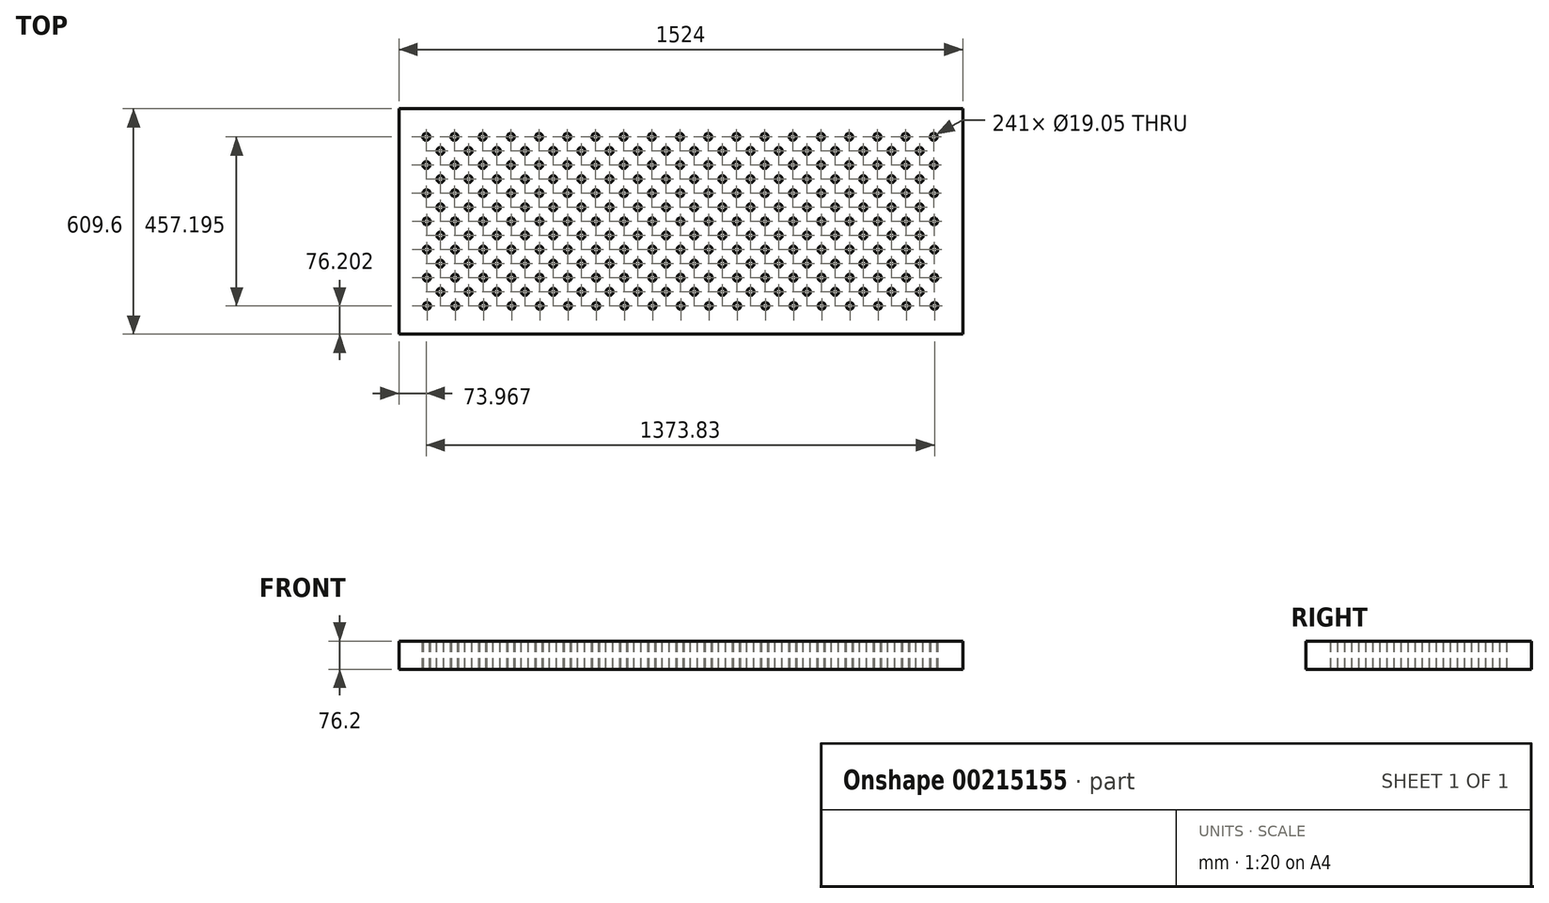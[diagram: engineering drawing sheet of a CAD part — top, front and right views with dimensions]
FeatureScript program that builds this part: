
annotation { "Feature Type Name" : "Feature", "Feature Type Description" : "" }
export const myFeature = defineFeature(function(context is Context, id is Id, definition is map)
    precondition{}
    {
        {
            var Q0;
            Q0=qCreatedBy(makeId("Top.planeOp"),FACE);
            var sketch = newSketch(context, id + "F0", { "sketchPlane" : qUnion([Q0])});
            skLineSegment(sketch, "E0.bottom", {"start": v(732.78, -488.74) * mm, "end": v(-791.22, -488.74) * mm});
            skLineSegment(sketch, "E0.top", {"start": v(732.78, 120.86) * mm, "end": v(-791.22, 120.86) * mm});
            skLineSegment(sketch, "E0.left", {"start": v(732.78, -488.74) * mm, "end": v(732.78, 120.86) * mm});
            skLineSegment(sketch, "E0.right", {"start": v(-791.22, -488.74) * mm, "end": v(-791.22, 120.86) * mm});
            skCircle(sketch, "E1", {"center": v(-715.02, -412.54) * mm, "radius": 9.53 * mm});
            skCircle(sketch, "E2.0.1.0", {"center": v(-715.4, -336.34) * mm, "radius": 9.53 * mm});
            skCircle(sketch, "E2.0.2.0", {"center": v(-715.77, -260.14) * mm, "radius": 9.53 * mm});
            skCircle(sketch, "E2.0.3.0", {"center": v(-716.14, -183.94) * mm, "radius": 9.53 * mm});
            skCircle(sketch, "E2.0.4.0", {"center": v(-716.5, -107.74) * mm, "radius": 9.53 * mm});
            skCircle(sketch, "E2.0.5.0", {"center": v(-716.88, -31.54) * mm, "radius": 9.53 * mm});
            skCircle(sketch, "E2.0.6.0", {"center": v(-717.25, 44.66) * mm, "radius": 9.53 * mm});
            skCircle(sketch, "E2.1.0.0", {"center": v(-638.82, -412.54) * mm, "radius": 9.53 * mm});
            skCircle(sketch, "E2.1.1.0", {"center": v(-639.2, -336.34) * mm, "radius": 9.53 * mm});
            skCircle(sketch, "E2.1.2.0", {"center": v(-639.57, -260.14) * mm, "radius": 9.53 * mm});
            skCircle(sketch, "E2.1.3.0", {"center": v(-639.94, -183.94) * mm, "radius": 9.53 * mm});
            skCircle(sketch, "E2.1.4.0", {"center": v(-640.3, -107.74) * mm, "radius": 9.53 * mm});
            skCircle(sketch, "E2.1.5.0", {"center": v(-640.68, -31.54) * mm, "radius": 9.53 * mm});
            skCircle(sketch, "E2.1.6.0", {"center": v(-641.05, 44.66) * mm, "radius": 9.53 * mm});
            skCircle(sketch, "E2.2.0.0", {"center": v(-562.62, -412.54) * mm, "radius": 9.53 * mm});
            skCircle(sketch, "E2.2.1.0", {"center": v(-563, -336.34) * mm, "radius": 9.53 * mm});
            skCircle(sketch, "E2.2.2.0", {"center": v(-563.37, -260.14) * mm, "radius": 9.53 * mm});
            skCircle(sketch, "E2.2.3.0", {"center": v(-563.74, -183.94) * mm, "radius": 9.53 * mm});
            skCircle(sketch, "E2.2.4.0", {"center": v(-564.1, -107.74) * mm, "radius": 9.53 * mm});
            skCircle(sketch, "E2.2.5.0", {"center": v(-564.48, -31.54) * mm, "radius": 9.53 * mm});
            skCircle(sketch, "E2.2.6.0", {"center": v(-564.85, 44.66) * mm, "radius": 9.53 * mm});
            skLineSegment(sketch, "E2.direction1", {"start": v(-715.02, -412.54) * mm, "end": v(-638.82, -412.54) * mm, "construction": true});
            skLineSegment(sketch, "E2.direction2", {"start": v(-715.02, -412.54) * mm, "end": v(-715.4, -336.34) * mm, "construction": true});
            skCircle(sketch, "E3.0.3.0", {"center": v(-486.42, -412.54) * mm, "radius": 9.53 * mm});
            skCircle(sketch, "E3.0.3.1", {"center": v(-486.8, -336.34) * mm, "radius": 9.53 * mm});
            skCircle(sketch, "E3.0.3.2", {"center": v(-487.17, -260.14) * mm, "radius": 9.53 * mm});
            skCircle(sketch, "E3.0.3.3", {"center": v(-487.54, -183.94) * mm, "radius": 9.53 * mm});
            skCircle(sketch, "E3.0.3.4", {"center": v(-487.9, -107.74) * mm, "radius": 9.53 * mm});
            skCircle(sketch, "E3.0.3.5", {"center": v(-488.28, -31.54) * mm, "radius": 9.53 * mm});
            skCircle(sketch, "E3.0.3.6", {"center": v(-488.65, 44.66) * mm, "radius": 9.53 * mm});
            skCircle(sketch, "E3.0.4.0", {"center": v(-410.22, -412.54) * mm, "radius": 9.53 * mm});
            skCircle(sketch, "E3.0.4.1", {"center": v(-410.6, -336.34) * mm, "radius": 9.53 * mm});
            skCircle(sketch, "E3.0.4.2", {"center": v(-410.97, -260.14) * mm, "radius": 9.53 * mm});
            skCircle(sketch, "E3.0.4.3", {"center": v(-411.34, -183.94) * mm, "radius": 9.53 * mm});
            skCircle(sketch, "E3.0.4.4", {"center": v(-411.7, -107.74) * mm, "radius": 9.53 * mm});
            skCircle(sketch, "E3.0.4.5", {"center": v(-412.08, -31.54) * mm, "radius": 9.53 * mm});
            skCircle(sketch, "E3.0.4.6", {"center": v(-412.45, 44.66) * mm, "radius": 9.53 * mm});
            skCircle(sketch, "E3.0.5.0", {"center": v(-334.02, -412.54) * mm, "radius": 9.53 * mm});
            skCircle(sketch, "E3.0.5.1", {"center": v(-334.4, -336.34) * mm, "radius": 9.53 * mm});
            skCircle(sketch, "E3.0.5.2", {"center": v(-334.77, -260.14) * mm, "radius": 9.53 * mm});
            skCircle(sketch, "E3.0.5.3", {"center": v(-335.14, -183.94) * mm, "radius": 9.53 * mm});
            skCircle(sketch, "E3.0.5.4", {"center": v(-335.5, -107.74) * mm, "radius": 9.53 * mm});
            skCircle(sketch, "E3.0.5.5", {"center": v(-335.88, -31.54) * mm, "radius": 9.53 * mm});
            skCircle(sketch, "E3.0.5.6", {"center": v(-336.25, 44.66) * mm, "radius": 9.53 * mm});
            skCircle(sketch, "E3.0.6.0", {"center": v(-257.82, -412.54) * mm, "radius": 9.53 * mm});
            skCircle(sketch, "E3.0.6.1", {"center": v(-258.2, -336.34) * mm, "radius": 9.53 * mm});
            skCircle(sketch, "E3.0.6.2", {"center": v(-258.57, -260.14) * mm, "radius": 9.53 * mm});
            skCircle(sketch, "E3.0.6.3", {"center": v(-258.94, -183.94) * mm, "radius": 9.53 * mm});
            skCircle(sketch, "E3.0.6.4", {"center": v(-259.3, -107.74) * mm, "radius": 9.53 * mm});
            skCircle(sketch, "E3.0.6.5", {"center": v(-259.68, -31.54) * mm, "radius": 9.53 * mm});
            skCircle(sketch, "E3.0.6.6", {"center": v(-260.05, 44.66) * mm, "radius": 9.53 * mm});
            skCircle(sketch, "E3.0.7.0", {"center": v(-181.62, -412.54) * mm, "radius": 9.53 * mm});
            skCircle(sketch, "E3.0.7.1", {"center": v(-182, -336.34) * mm, "radius": 9.53 * mm});
            skCircle(sketch, "E3.0.7.2", {"center": v(-182.37, -260.14) * mm, "radius": 9.53 * mm});
            skCircle(sketch, "E3.0.7.3", {"center": v(-182.74, -183.94) * mm, "radius": 9.53 * mm});
            skCircle(sketch, "E3.0.7.4", {"center": v(-183.1, -107.74) * mm, "radius": 9.53 * mm});
            skCircle(sketch, "E3.0.7.5", {"center": v(-183.48, -31.54) * mm, "radius": 9.53 * mm});
            skCircle(sketch, "E3.0.7.6", {"center": v(-183.85, 44.66) * mm, "radius": 9.53 * mm});
            skCircle(sketch, "E3.0.8.0", {"center": v(-105.42, -412.54) * mm, "radius": 9.53 * mm});
            skCircle(sketch, "E3.0.8.1", {"center": v(-105.8, -336.34) * mm, "radius": 9.53 * mm});
            skCircle(sketch, "E3.0.8.2", {"center": v(-106.17, -260.14) * mm, "radius": 9.53 * mm});
            skCircle(sketch, "E3.0.8.3", {"center": v(-106.54, -183.94) * mm, "radius": 9.53 * mm});
            skCircle(sketch, "E3.0.8.4", {"center": v(-106.9, -107.74) * mm, "radius": 9.53 * mm});
            skCircle(sketch, "E3.0.8.5", {"center": v(-107.28, -31.54) * mm, "radius": 9.53 * mm});
            skCircle(sketch, "E3.0.8.6", {"center": v(-107.65, 44.66) * mm, "radius": 9.53 * mm});
            skCircle(sketch, "E3.0.9.0", {"center": v(-29.22, -412.54) * mm, "radius": 9.53 * mm});
            skCircle(sketch, "E3.0.9.1", {"center": v(-29.6, -336.34) * mm, "radius": 9.53 * mm});
            skCircle(sketch, "E3.0.9.2", {"center": v(-29.97, -260.14) * mm, "radius": 9.53 * mm});
            skCircle(sketch, "E3.0.9.3", {"center": v(-30.34, -183.94) * mm, "radius": 9.53 * mm});
            skCircle(sketch, "E3.0.9.4", {"center": v(-30.7, -107.74) * mm, "radius": 9.53 * mm});
            skCircle(sketch, "E3.0.9.5", {"center": v(-31.08, -31.54) * mm, "radius": 9.53 * mm});
            skCircle(sketch, "E3.0.9.6", {"center": v(-31.45, 44.66) * mm, "radius": 9.53 * mm});
            skCircle(sketch, "E3.0.10.0", {"center": v(46.98, -412.54) * mm, "radius": 9.53 * mm});
            skCircle(sketch, "E3.0.10.1", {"center": v(46.6, -336.34) * mm, "radius": 9.53 * mm});
            skCircle(sketch, "E3.0.10.2", {"center": v(46.23, -260.14) * mm, "radius": 9.53 * mm});
            skCircle(sketch, "E3.0.10.3", {"center": v(45.86, -183.94) * mm, "radius": 9.53 * mm});
            skCircle(sketch, "E3.0.10.4", {"center": v(45.5, -107.74) * mm, "radius": 9.53 * mm});
            skCircle(sketch, "E3.0.10.5", {"center": v(45.12, -31.54) * mm, "radius": 9.53 * mm});
            skCircle(sketch, "E3.0.10.6", {"center": v(44.75, 44.66) * mm, "radius": 9.53 * mm});
            skCircle(sketch, "E3.0.11.0", {"center": v(123.18, -412.54) * mm, "radius": 9.53 * mm});
            skCircle(sketch, "E3.0.11.1", {"center": v(122.8, -336.34) * mm, "radius": 9.53 * mm});
            skCircle(sketch, "E3.0.11.2", {"center": v(122.43, -260.14) * mm, "radius": 9.53 * mm});
            skCircle(sketch, "E3.0.11.3", {"center": v(122.06, -183.94) * mm, "radius": 9.53 * mm});
            skCircle(sketch, "E3.0.11.4", {"center": v(121.7, -107.74) * mm, "radius": 9.53 * mm});
            skCircle(sketch, "E3.0.11.5", {"center": v(121.32, -31.54) * mm, "radius": 9.53 * mm});
            skCircle(sketch, "E3.0.11.6", {"center": v(120.95, 44.66) * mm, "radius": 9.53 * mm});
            skCircle(sketch, "E3.0.12.0", {"center": v(199.38, -412.54) * mm, "radius": 9.53 * mm});
            skCircle(sketch, "E3.0.12.1", {"center": v(199, -336.34) * mm, "radius": 9.53 * mm});
            skCircle(sketch, "E3.0.12.2", {"center": v(198.63, -260.14) * mm, "radius": 9.53 * mm});
            skCircle(sketch, "E3.0.12.3", {"center": v(198.26, -183.94) * mm, "radius": 9.53 * mm});
            skCircle(sketch, "E3.0.12.4", {"center": v(197.9, -107.74) * mm, "radius": 9.53 * mm});
            skCircle(sketch, "E3.0.12.5", {"center": v(197.52, -31.54) * mm, "radius": 9.53 * mm});
            skCircle(sketch, "E3.0.12.6", {"center": v(197.15, 44.66) * mm, "radius": 9.53 * mm});
            skCircle(sketch, "E3.0.13.0", {"center": v(275.58, -412.54) * mm, "radius": 9.53 * mm});
            skCircle(sketch, "E3.0.13.1", {"center": v(275.2, -336.34) * mm, "radius": 9.53 * mm});
            skCircle(sketch, "E3.0.13.2", {"center": v(274.83, -260.14) * mm, "radius": 9.53 * mm});
            skCircle(sketch, "E3.0.13.3", {"center": v(274.46, -183.94) * mm, "radius": 9.53 * mm});
            skCircle(sketch, "E3.0.13.4", {"center": v(274.1, -107.74) * mm, "radius": 9.53 * mm});
            skCircle(sketch, "E3.0.13.5", {"center": v(273.72, -31.54) * mm, "radius": 9.53 * mm});
            skCircle(sketch, "E3.0.13.6", {"center": v(273.35, 44.66) * mm, "radius": 9.53 * mm});
            skCircle(sketch, "E3.0.14.0", {"center": v(351.78, -412.54) * mm, "radius": 9.53 * mm});
            skCircle(sketch, "E3.0.14.1", {"center": v(351.4, -336.34) * mm, "radius": 9.53 * mm});
            skCircle(sketch, "E3.0.14.2", {"center": v(351.03, -260.14) * mm, "radius": 9.53 * mm});
            skCircle(sketch, "E3.0.14.3", {"center": v(350.66, -183.94) * mm, "radius": 9.53 * mm});
            skCircle(sketch, "E3.0.14.4", {"center": v(350.3, -107.74) * mm, "radius": 9.53 * mm});
            skCircle(sketch, "E3.0.14.5", {"center": v(349.92, -31.54) * mm, "radius": 9.53 * mm});
            skCircle(sketch, "E3.0.14.6", {"center": v(349.55, 44.66) * mm, "radius": 9.53 * mm});
            skCircle(sketch, "E3.0.15.0", {"center": v(427.98, -412.54) * mm, "radius": 9.53 * mm});
            skCircle(sketch, "E3.0.15.1", {"center": v(427.6, -336.34) * mm, "radius": 9.53 * mm});
            skCircle(sketch, "E3.0.15.2", {"center": v(427.23, -260.14) * mm, "radius": 9.53 * mm});
            skCircle(sketch, "E3.0.15.3", {"center": v(426.86, -183.94) * mm, "radius": 9.53 * mm});
            skCircle(sketch, "E3.0.15.4", {"center": v(426.5, -107.74) * mm, "radius": 9.53 * mm});
            skCircle(sketch, "E3.0.15.5", {"center": v(426.12, -31.54) * mm, "radius": 9.53 * mm});
            skCircle(sketch, "E3.0.15.6", {"center": v(425.75, 44.66) * mm, "radius": 9.53 * mm});
            skCircle(sketch, "E3.0.16.0", {"center": v(504.18, -412.54) * mm, "radius": 9.53 * mm});
            skCircle(sketch, "E3.0.16.1", {"center": v(503.8, -336.34) * mm, "radius": 9.53 * mm});
            skCircle(sketch, "E3.0.16.2", {"center": v(503.43, -260.14) * mm, "radius": 9.53 * mm});
            skCircle(sketch, "E3.0.16.3", {"center": v(503.06, -183.94) * mm, "radius": 9.53 * mm});
            skCircle(sketch, "E3.0.16.4", {"center": v(502.7, -107.74) * mm, "radius": 9.53 * mm});
            skCircle(sketch, "E3.0.16.5", {"center": v(502.32, -31.54) * mm, "radius": 9.53 * mm});
            skCircle(sketch, "E3.0.16.6", {"center": v(501.95, 44.66) * mm, "radius": 9.53 * mm});
            skCircle(sketch, "E3.0.17.0", {"center": v(580.38, -412.54) * mm, "radius": 9.53 * mm});
            skCircle(sketch, "E3.0.17.1", {"center": v(580, -336.34) * mm, "radius": 9.53 * mm});
            skCircle(sketch, "E3.0.17.2", {"center": v(579.63, -260.14) * mm, "radius": 9.53 * mm});
            skCircle(sketch, "E3.0.17.3", {"center": v(579.26, -183.94) * mm, "radius": 9.53 * mm});
            skCircle(sketch, "E3.0.17.4", {"center": v(578.9, -107.74) * mm, "radius": 9.53 * mm});
            skCircle(sketch, "E3.0.17.5", {"center": v(578.52, -31.54) * mm, "radius": 9.53 * mm});
            skCircle(sketch, "E3.0.17.6", {"center": v(578.15, 44.66) * mm, "radius": 9.53 * mm});
            skCircle(sketch, "E3.0.18.0", {"center": v(656.58, -412.54) * mm, "radius": 9.53 * mm});
            skCircle(sketch, "E3.0.18.1", {"center": v(656.2, -336.34) * mm, "radius": 9.53 * mm});
            skCircle(sketch, "E3.0.18.2", {"center": v(655.83, -260.14) * mm, "radius": 9.53 * mm});
            skCircle(sketch, "E3.0.18.3", {"center": v(655.46, -183.94) * mm, "radius": 9.53 * mm});
            skCircle(sketch, "E3.0.18.4", {"center": v(655.1, -107.74) * mm, "radius": 9.53 * mm});
            skCircle(sketch, "E3.0.18.5", {"center": v(654.72, -31.54) * mm, "radius": 9.53 * mm});
            skCircle(sketch, "E3.0.18.6", {"center": v(654.35, 44.66) * mm, "radius": 9.53 * mm});
            skLineSegment(sketch, "E4", {"start": v(-641.05, 44.66) * mm, "end": v(-716.88, -31.54) * mm, "construction": true});
            skLineSegment(sketch, "E5", {"start": v(-640.68, -31.54) * mm, "end": v(-717.25, 44.66) * mm, "construction": true});
            skCircle(sketch, "E6", {"center": v(-678.97, 6.56) * mm, "radius": 9.52 * mm});
            skCircle(sketch, "E7.0.1.0", {"center": v(-678.97, -69.64) * mm, "radius": 9.52 * mm});
            skCircle(sketch, "E7.0.2.0", {"center": v(-678.97, -145.84) * mm, "radius": 9.52 * mm});
            skCircle(sketch, "E7.0.3.0", {"center": v(-678.97, -222.04) * mm, "radius": 9.52 * mm});
            skCircle(sketch, "E7.0.4.0", {"center": v(-678.97, -298.24) * mm, "radius": 9.52 * mm});
            skCircle(sketch, "E7.0.5.0", {"center": v(-678.97, -374.44) * mm, "radius": 9.52 * mm});
            skCircle(sketch, "E7.1.0.0", {"center": v(-602.77, 6.56) * mm, "radius": 9.52 * mm});
            skCircle(sketch, "E7.1.1.0", {"center": v(-602.77, -69.64) * mm, "radius": 9.52 * mm});
            skCircle(sketch, "E7.1.2.0", {"center": v(-602.77, -145.84) * mm, "radius": 9.52 * mm});
            skCircle(sketch, "E7.1.3.0", {"center": v(-602.77, -222.04) * mm, "radius": 9.52 * mm});
            skCircle(sketch, "E7.1.4.0", {"center": v(-602.77, -298.24) * mm, "radius": 9.52 * mm});
            skCircle(sketch, "E7.1.5.0", {"center": v(-602.77, -374.44) * mm, "radius": 9.52 * mm});
            skCircle(sketch, "E7.2.0.0", {"center": v(-526.57, 6.56) * mm, "radius": 9.52 * mm});
            skCircle(sketch, "E7.2.1.0", {"center": v(-526.57, -69.64) * mm, "radius": 9.52 * mm});
            skCircle(sketch, "E7.2.2.0", {"center": v(-526.57, -145.84) * mm, "radius": 9.52 * mm});
            skCircle(sketch, "E7.2.3.0", {"center": v(-526.57, -222.04) * mm, "radius": 9.52 * mm});
            skCircle(sketch, "E7.2.4.0", {"center": v(-526.57, -298.24) * mm, "radius": 9.52 * mm});
            skCircle(sketch, "E7.2.5.0", {"center": v(-526.57, -374.44) * mm, "radius": 9.52 * mm});
            skCircle(sketch, "E7.3.0.0", {"center": v(-450.37, 6.56) * mm, "radius": 9.52 * mm});
            skCircle(sketch, "E7.3.1.0", {"center": v(-450.37, -69.64) * mm, "radius": 9.52 * mm});
            skCircle(sketch, "E7.3.2.0", {"center": v(-450.37, -145.84) * mm, "radius": 9.52 * mm});
            skCircle(sketch, "E7.3.3.0", {"center": v(-450.37, -222.04) * mm, "radius": 9.52 * mm});
            skCircle(sketch, "E7.3.4.0", {"center": v(-450.37, -298.24) * mm, "radius": 9.52 * mm});
            skCircle(sketch, "E7.3.5.0", {"center": v(-450.37, -374.44) * mm, "radius": 9.52 * mm});
            skCircle(sketch, "E7.4.0.0", {"center": v(-374.17, 6.56) * mm, "radius": 9.52 * mm});
            skCircle(sketch, "E7.4.1.0", {"center": v(-374.17, -69.64) * mm, "radius": 9.52 * mm});
            skCircle(sketch, "E7.4.2.0", {"center": v(-374.17, -145.84) * mm, "radius": 9.52 * mm});
            skCircle(sketch, "E7.4.3.0", {"center": v(-374.17, -222.04) * mm, "radius": 9.52 * mm});
            skCircle(sketch, "E7.4.4.0", {"center": v(-374.17, -298.24) * mm, "radius": 9.52 * mm});
            skCircle(sketch, "E7.4.5.0", {"center": v(-374.17, -374.44) * mm, "radius": 9.52 * mm});
            skCircle(sketch, "E7.5.0.0", {"center": v(-297.97, 6.56) * mm, "radius": 9.52 * mm});
            skCircle(sketch, "E7.5.1.0", {"center": v(-297.97, -69.64) * mm, "radius": 9.52 * mm});
            skCircle(sketch, "E7.5.2.0", {"center": v(-297.97, -145.84) * mm, "radius": 9.52 * mm});
            skCircle(sketch, "E7.5.3.0", {"center": v(-297.97, -222.04) * mm, "radius": 9.52 * mm});
            skCircle(sketch, "E7.5.4.0", {"center": v(-297.97, -298.24) * mm, "radius": 9.52 * mm});
            skCircle(sketch, "E7.5.5.0", {"center": v(-297.97, -374.44) * mm, "radius": 9.52 * mm});
            skCircle(sketch, "E7.6.0.0", {"center": v(-221.77, 6.56) * mm, "radius": 9.52 * mm});
            skCircle(sketch, "E7.6.1.0", {"center": v(-221.77, -69.64) * mm, "radius": 9.52 * mm});
            skCircle(sketch, "E7.6.2.0", {"center": v(-221.77, -145.84) * mm, "radius": 9.52 * mm});
            skCircle(sketch, "E7.6.3.0", {"center": v(-221.77, -222.04) * mm, "radius": 9.52 * mm});
            skCircle(sketch, "E7.6.4.0", {"center": v(-221.77, -298.24) * mm, "radius": 9.52 * mm});
            skCircle(sketch, "E7.6.5.0", {"center": v(-221.77, -374.44) * mm, "radius": 9.52 * mm});
            skCircle(sketch, "E7.7.0.0", {"center": v(-145.57, 6.56) * mm, "radius": 9.52 * mm});
            skCircle(sketch, "E7.7.1.0", {"center": v(-145.57, -69.64) * mm, "radius": 9.52 * mm});
            skCircle(sketch, "E7.7.2.0", {"center": v(-145.57, -145.84) * mm, "radius": 9.52 * mm});
            skCircle(sketch, "E7.7.3.0", {"center": v(-145.57, -222.04) * mm, "radius": 9.52 * mm});
            skCircle(sketch, "E7.7.4.0", {"center": v(-145.57, -298.24) * mm, "radius": 9.52 * mm});
            skCircle(sketch, "E7.7.5.0", {"center": v(-145.57, -374.44) * mm, "radius": 9.52 * mm});
            skCircle(sketch, "E7.8.0.0", {"center": v(-69.37, 6.56) * mm, "radius": 9.52 * mm});
            skCircle(sketch, "E7.8.1.0", {"center": v(-69.37, -69.64) * mm, "radius": 9.52 * mm});
            skCircle(sketch, "E7.8.2.0", {"center": v(-69.37, -145.84) * mm, "radius": 9.52 * mm});
            skCircle(sketch, "E7.8.3.0", {"center": v(-69.37, -222.04) * mm, "radius": 9.52 * mm});
            skCircle(sketch, "E7.8.4.0", {"center": v(-69.37, -298.24) * mm, "radius": 9.52 * mm});
            skCircle(sketch, "E7.8.5.0", {"center": v(-69.37, -374.44) * mm, "radius": 9.52 * mm});
            skCircle(sketch, "E7.9.0.0", {"center": v(6.83, 6.56) * mm, "radius": 9.52 * mm});
            skCircle(sketch, "E7.9.1.0", {"center": v(6.83, -69.64) * mm, "radius": 9.52 * mm});
            skCircle(sketch, "E7.9.2.0", {"center": v(6.83, -145.84) * mm, "radius": 9.52 * mm});
            skCircle(sketch, "E7.9.3.0", {"center": v(6.83, -222.04) * mm, "radius": 9.52 * mm});
            skCircle(sketch, "E7.9.4.0", {"center": v(6.83, -298.24) * mm, "radius": 9.52 * mm});
            skCircle(sketch, "E7.9.5.0", {"center": v(6.83, -374.44) * mm, "radius": 9.52 * mm});
            skCircle(sketch, "E7.10.0.0", {"center": v(83.03, 6.56) * mm, "radius": 9.52 * mm});
            skCircle(sketch, "E7.10.1.0", {"center": v(83.03, -69.64) * mm, "radius": 9.52 * mm});
            skCircle(sketch, "E7.10.2.0", {"center": v(83.03, -145.84) * mm, "radius": 9.52 * mm});
            skCircle(sketch, "E7.10.3.0", {"center": v(83.03, -222.04) * mm, "radius": 9.52 * mm});
            skCircle(sketch, "E7.10.4.0", {"center": v(83.03, -298.24) * mm, "radius": 9.52 * mm});
            skCircle(sketch, "E7.10.5.0", {"center": v(83.03, -374.44) * mm, "radius": 9.52 * mm});
            skCircle(sketch, "E7.11.0.0", {"center": v(159.23, 6.56) * mm, "radius": 9.52 * mm});
            skCircle(sketch, "E7.11.1.0", {"center": v(159.23, -69.64) * mm, "radius": 9.52 * mm});
            skCircle(sketch, "E7.11.2.0", {"center": v(159.23, -145.84) * mm, "radius": 9.52 * mm});
            skCircle(sketch, "E7.11.3.0", {"center": v(159.23, -222.04) * mm, "radius": 9.52 * mm});
            skCircle(sketch, "E7.11.4.0", {"center": v(159.23, -298.24) * mm, "radius": 9.52 * mm});
            skCircle(sketch, "E7.11.5.0", {"center": v(159.23, -374.44) * mm, "radius": 9.52 * mm});
            skCircle(sketch, "E7.12.0.0", {"center": v(235.43, 6.56) * mm, "radius": 9.52 * mm});
            skCircle(sketch, "E7.12.1.0", {"center": v(235.43, -69.64) * mm, "radius": 9.52 * mm});
            skCircle(sketch, "E7.12.2.0", {"center": v(235.43, -145.84) * mm, "radius": 9.52 * mm});
            skCircle(sketch, "E7.12.3.0", {"center": v(235.43, -222.04) * mm, "radius": 9.52 * mm});
            skCircle(sketch, "E7.12.4.0", {"center": v(235.43, -298.24) * mm, "radius": 9.52 * mm});
            skCircle(sketch, "E7.12.5.0", {"center": v(235.43, -374.44) * mm, "radius": 9.52 * mm});
            skCircle(sketch, "E7.13.0.0", {"center": v(311.63, 6.56) * mm, "radius": 9.52 * mm});
            skCircle(sketch, "E7.13.1.0", {"center": v(311.63, -69.64) * mm, "radius": 9.52 * mm});
            skCircle(sketch, "E7.13.2.0", {"center": v(311.63, -145.84) * mm, "radius": 9.52 * mm});
            skCircle(sketch, "E7.13.3.0", {"center": v(311.63, -222.04) * mm, "radius": 9.52 * mm});
            skCircle(sketch, "E7.13.4.0", {"center": v(311.63, -298.24) * mm, "radius": 9.52 * mm});
            skCircle(sketch, "E7.13.5.0", {"center": v(311.63, -374.44) * mm, "radius": 9.52 * mm});
            skCircle(sketch, "E7.14.0.0", {"center": v(387.83, 6.56) * mm, "radius": 9.52 * mm});
            skCircle(sketch, "E7.14.1.0", {"center": v(387.83, -69.64) * mm, "radius": 9.52 * mm});
            skCircle(sketch, "E7.14.2.0", {"center": v(387.83, -145.84) * mm, "radius": 9.52 * mm});
            skCircle(sketch, "E7.14.3.0", {"center": v(387.83, -222.04) * mm, "radius": 9.52 * mm});
            skCircle(sketch, "E7.14.4.0", {"center": v(387.83, -298.24) * mm, "radius": 9.52 * mm});
            skCircle(sketch, "E7.14.5.0", {"center": v(387.83, -374.44) * mm, "radius": 9.52 * mm});
            skCircle(sketch, "E7.15.0.0", {"center": v(464.03, 6.56) * mm, "radius": 9.52 * mm});
            skCircle(sketch, "E7.15.1.0", {"center": v(464.03, -69.64) * mm, "radius": 9.52 * mm});
            skCircle(sketch, "E7.15.2.0", {"center": v(464.03, -145.84) * mm, "radius": 9.52 * mm});
            skCircle(sketch, "E7.15.3.0", {"center": v(464.03, -222.04) * mm, "radius": 9.52 * mm});
            skCircle(sketch, "E7.15.4.0", {"center": v(464.03, -298.24) * mm, "radius": 9.52 * mm});
            skCircle(sketch, "E7.15.5.0", {"center": v(464.03, -374.44) * mm, "radius": 9.52 * mm});
            skCircle(sketch, "E7.16.0.0", {"center": v(540.23, 6.56) * mm, "radius": 9.52 * mm});
            skCircle(sketch, "E7.16.1.0", {"center": v(540.23, -69.64) * mm, "radius": 9.52 * mm});
            skCircle(sketch, "E7.16.2.0", {"center": v(540.23, -145.84) * mm, "radius": 9.52 * mm});
            skCircle(sketch, "E7.16.3.0", {"center": v(540.23, -222.04) * mm, "radius": 9.52 * mm});
            skCircle(sketch, "E7.16.4.0", {"center": v(540.23, -298.24) * mm, "radius": 9.52 * mm});
            skCircle(sketch, "E7.16.5.0", {"center": v(540.23, -374.44) * mm, "radius": 9.52 * mm});
            skCircle(sketch, "E7.17.0.0", {"center": v(616.43, 6.56) * mm, "radius": 9.52 * mm});
            skCircle(sketch, "E7.17.1.0", {"center": v(616.43, -69.64) * mm, "radius": 9.52 * mm});
            skCircle(sketch, "E7.17.2.0", {"center": v(616.43, -145.84) * mm, "radius": 9.52 * mm});
            skCircle(sketch, "E7.17.3.0", {"center": v(616.43, -222.04) * mm, "radius": 9.52 * mm});
            skCircle(sketch, "E7.17.4.0", {"center": v(616.43, -298.24) * mm, "radius": 9.52 * mm});
            skCircle(sketch, "E7.17.5.0", {"center": v(616.43, -374.44) * mm, "radius": 9.52 * mm});
            skLineSegment(sketch, "E7.direction1", {"start": v(-678.97, 6.56) * mm, "end": v(-602.77, 6.56) * mm, "construction": true});
            skLineSegment(sketch, "E7.direction2", {"start": v(-678.97, 6.56) * mm, "end": v(-678.97, -69.64) * mm, "construction": true});
            skSolve(sketch);
        }
        {
            var Q0;
            Q0=makeQuery(id+"F0.imprint","IMPRINT",FACE,{"disambiguationData":[TD([[makeQuery(id+"F0.imprint","IMPRINT",EDGE,{"derivedFrom":sQuery(id+"F0.wireOp",EDGE,"E0.bottom")}),-1.0]])]});
            extrude(context, id + "F1", {"entities" : qUnion([Q0]), "oppositeDirection" : true, "depth" : 76.2 * mm});
        }
    });
